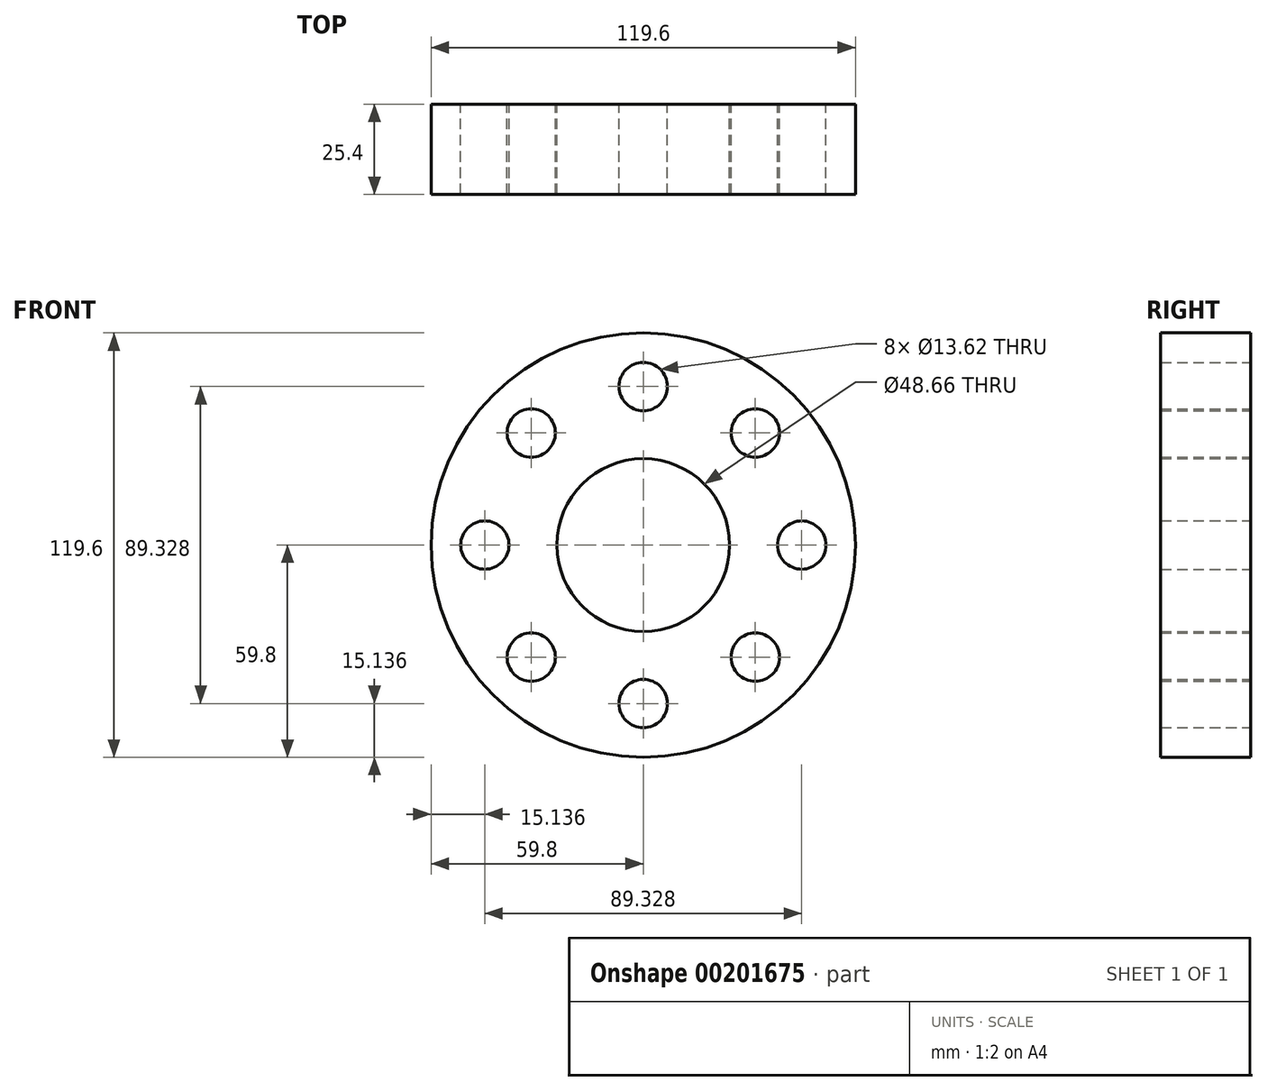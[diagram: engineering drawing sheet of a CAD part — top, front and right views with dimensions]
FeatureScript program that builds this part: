
annotation { "Feature Type Name" : "Feature", "Feature Type Description" : "" }
export const myFeature = defineFeature(function(context is Context, id is Id, definition is map)
    precondition{}
    {
        {
            var Q0;
            Q0=qCreatedBy(makeId("Front.planeOp"),FACE);
            var sketch = newSketch(context, id + "F0", { "sketchPlane" : qUnion([Q0])});
            skCircle(sketch, "E0", {"center": v(0, 0) * mm, "radius": 24.33 * mm});
            skCircle(sketch, "E1", {"center": v(0, 0) * mm, "radius": 59.8 * mm});
            skCircle(sketch, "E2", {"center": v(0, 44.66) * mm, "radius": 6.8 * mm});
            skCircle(sketch, "E3.1.0", {"center": v(-31.58, 31.58) * mm, "radius": 6.8 * mm});
            skCircle(sketch, "E3.2.0", {"center": v(-44.66, 0) * mm, "radius": 6.8 * mm});
            skCircle(sketch, "E3.3.0", {"center": v(-31.58, -31.58) * mm, "radius": 6.8 * mm});
            skCircle(sketch, "E3.4.0", {"center": v(0, -44.66) * mm, "radius": 6.8 * mm});
            skCircle(sketch, "E3.5.0", {"center": v(31.58, -31.58) * mm, "radius": 6.8 * mm});
            skCircle(sketch, "E3.6.0", {"center": v(44.66, 0) * mm, "radius": 6.8 * mm});
            skCircle(sketch, "E3.7.0", {"center": v(31.58, 31.58) * mm, "radius": 6.8 * mm});
            skSolve(sketch);
        }
        {
            var Q0;
            Q0=makeQuery(id+"F0.imprint","IMPRINT",FACE,{"disambiguationData":[TD([[makeQuery(id+"F0.imprint","IMPRINT",EDGE,{"derivedFrom":sQuery(id+"F0.wireOp",EDGE,"E0")}),-1.0]])]});
            extrude(context, id + "F1", {"entities" : qUnion([Q0]), "endBound" : BoundingType.SYMMETRIC, "depth" : 25.4 * mm});
        }
    });
